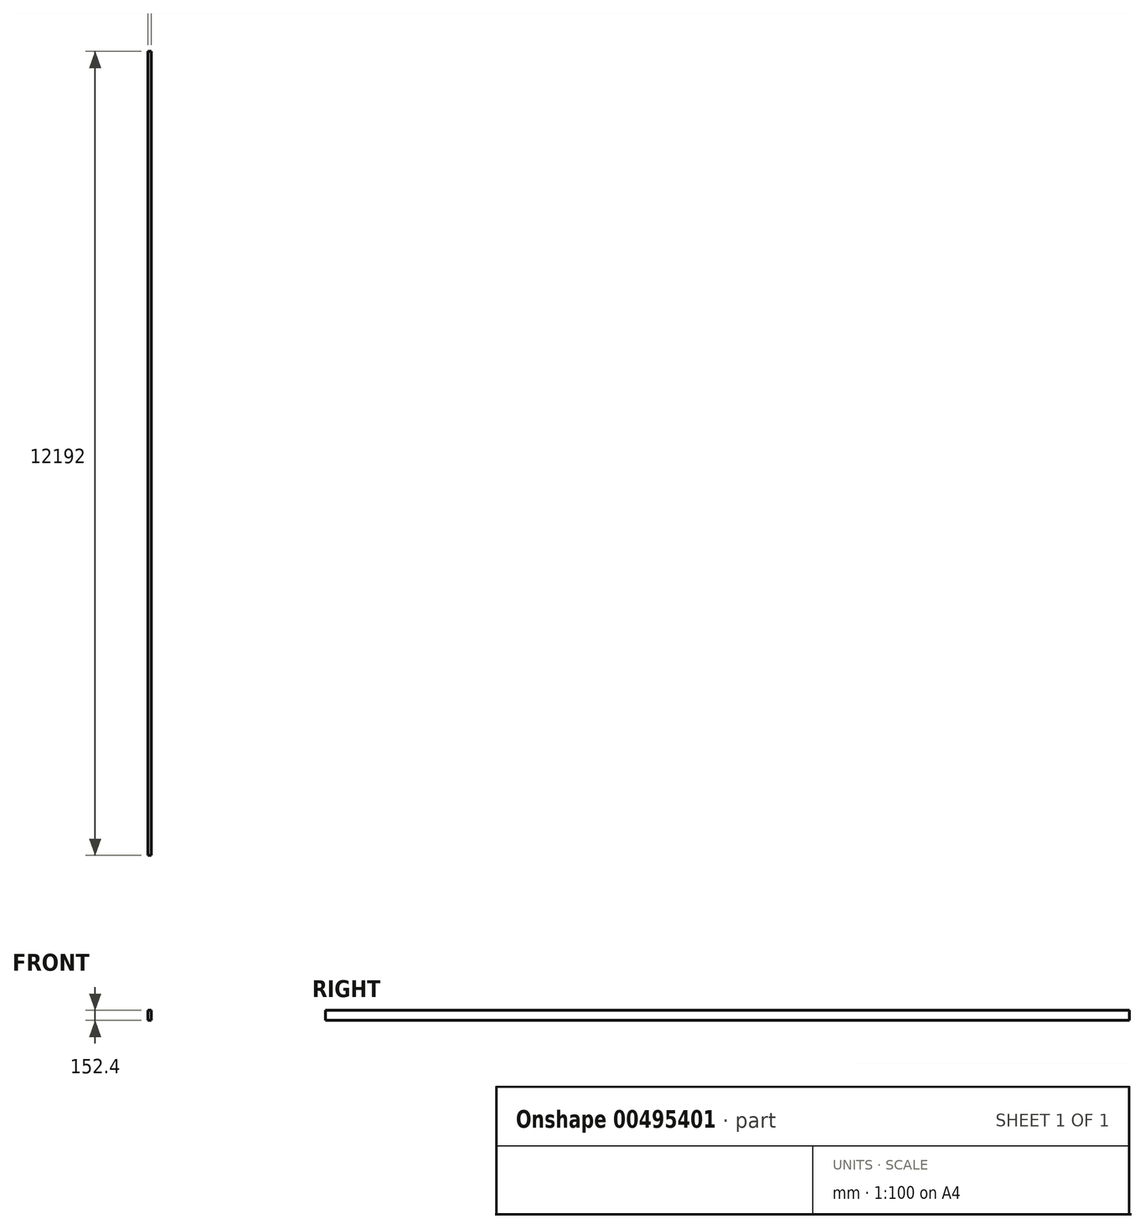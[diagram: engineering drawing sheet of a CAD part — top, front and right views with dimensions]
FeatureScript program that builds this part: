
annotation { "Feature Type Name" : "Feature", "Feature Type Description" : "" }
export const myFeature = defineFeature(function(context is Context, id is Id, definition is map)
    precondition{}
    {
        {
            var Q0;
            Q0=qCreatedBy(makeId("Front.planeOp"),FACE);
            var sketch = newSketch(context, id + "F0", { "sketchPlane" : qUnion([Q0])});
            skLineSegment(sketch, "E0.bottom", {"start": v(0, 0) * mm, "end": v(50.8, 0) * mm});
            skLineSegment(sketch, "E0.top", {"start": v(0, 152.4) * mm, "end": v(50.8, 152.4) * mm});
            skLineSegment(sketch, "E0.left", {"start": v(0, 0) * mm, "end": v(0, 152.4) * mm});
            skLineSegment(sketch, "E0.right", {"start": v(50.8, 0) * mm, "end": v(50.8, 152.4) * mm});
            skSolve(sketch);
        }
        {
            var Q0;
            Q0 = qSketchRegion(id + "F0", true);
            extrude(context, id + "F1", {"entities" : qUnion([Q0]), "depth" : 12192 * mm, "offsetDistance" : 25.4 * mm});
        }
    });
